# Revit family: PENEDERHighlinebreakout
name_source: partatom
category: Türen
units: mm (PartAtom-declared; Revit-internal decimal feet)

## family parameters
Basisbauteil = Wand
Beim Laden mit Abzugskörper schneiden = Nein
Gemeinsam genutzt = Nein
Immer vertikal = Ja
OmniClass-Nummer = 23.30.10.00
OmniClass-Titel = Doors
Raumberechnungspunkt = Ja

## types (1)
- PENEDERHighlinebreakout
    Antrieb Höhe = 200 mm  [stored 0.656168 ft]
    Antrieb Tiefe = 211 mm  [stored 0.692257 ft]
    Beschreibung = PENEDERHighlinebreakout
    Dicke = 96 mm  [stored 0.314961 ft]
    Feuerwiderstandsklasse = EI2 30-C
    Funktion = Innen
    Hersteller = PENEDER Bau-Elemente GmbH
    MAT_Antrieb = Pender - Metall 241-236-225
    MAT_Lackierung Randverbund = Peneder_Beschläge Edelstahl
    MAT_Schiebeflügel = Pender - Metall 241-236-225
    MAT_Verglasung = Pender - Glas
    Modell = PENEDERHighlinebreakout
    TB_Leitprodukt = PENEDERHighlinebreakout
    TB_Material = Stahl
    T_Aussentuer = Ja
    T_Bedienung = automatisch öffnen
    T_Brandschutz = EI2 30-C
    T_Fluegelanzahl = 2
    Typenkommentare = Automatikschibetür mit Brandschutz- und Fluchtfunktion
    Wandabschluss = Nach Basisbauteil

note: [stored X ft] marks values corroborated as IEEE doubles in the binary element streams (Revit-internal decimal feet)
